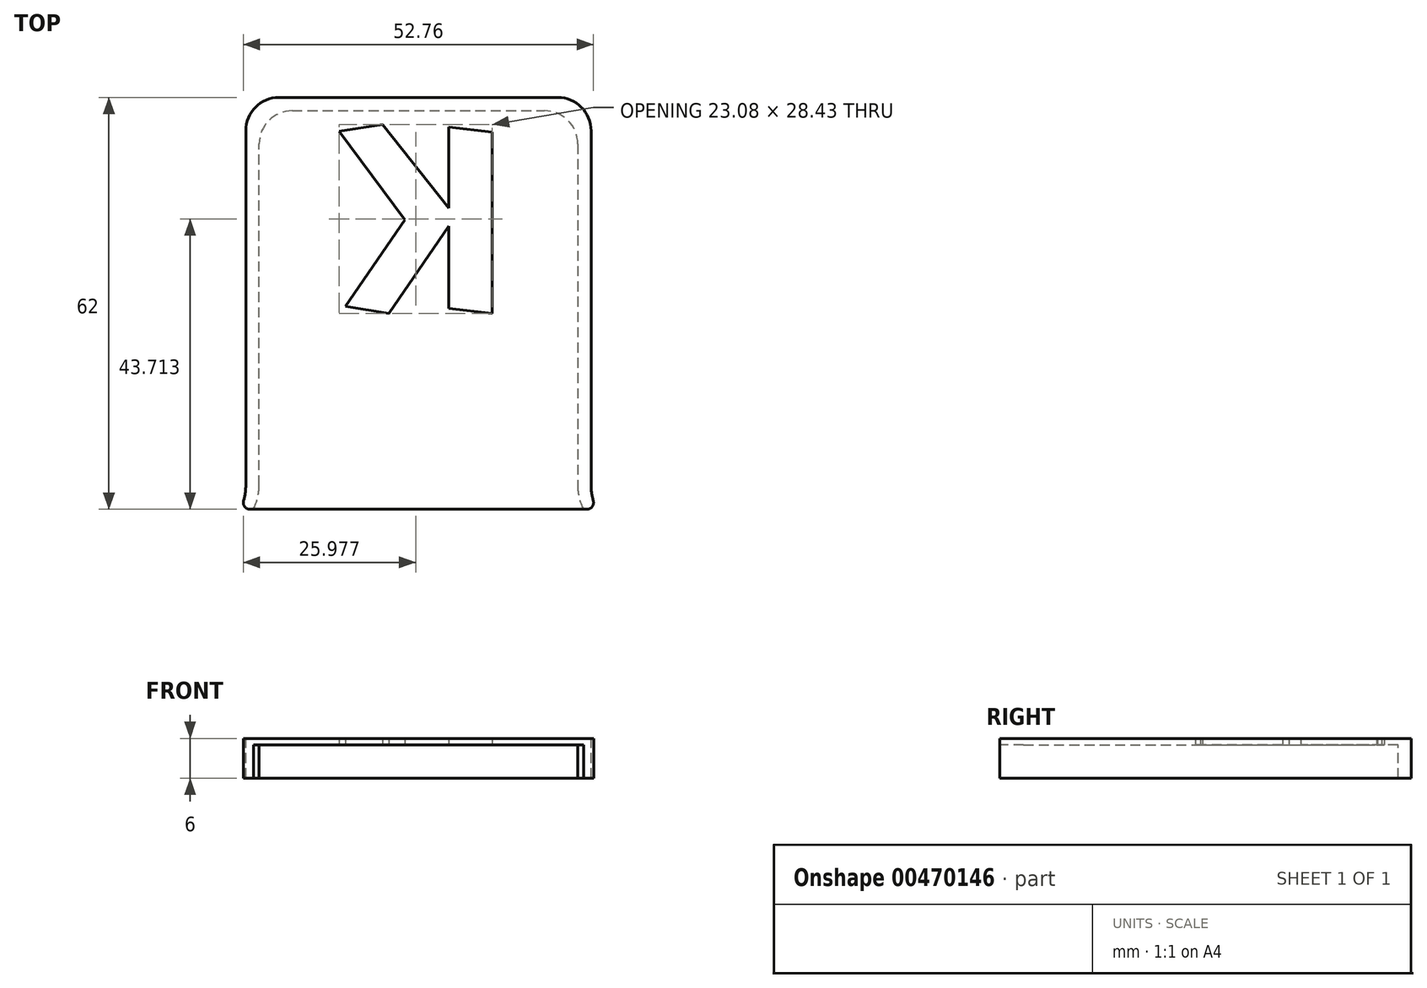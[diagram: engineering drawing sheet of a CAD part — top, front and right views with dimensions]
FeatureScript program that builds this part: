
annotation { "Feature Type Name" : "Feature", "Feature Type Description" : "" }
export const myFeature = defineFeature(function(context is Context, id is Id, definition is map)
    precondition{}
    {
        {
            var Q0;
            Q0=qCreatedBy(makeId("Top.planeOp"),FACE);
            var sketch = newSketch(context, id + "F0", { "sketchPlane" : qUnion([Q0])});
            skLineSegment(sketch, "E0", {"start": v(-24, 30) * mm, "end": v(24, 30) * mm});
            skLineSegment(sketch, "E1", {"start": v(24, 30) * mm, "end": v(24, -30) * mm});
            skLineSegment(sketch, "E2", {"start": v(24, -30) * mm, "end": v(-24, -30) * mm});
            skLineSegment(sketch, "E3", {"start": v(-24, -30) * mm, "end": v(-24, 30) * mm});
            skLineSegment(sketch, "E4", {"start": v(24, 30) * mm, "end": v(-24, -30) * mm, "construction": true});
            skLineSegment(sketch, "E5.MirrorCS", {"start": v(-26.5, -30) * mm, "end": v(-24, -20.3) * mm});
            skLineSegment(sketch, "E6.MirrorCS", {"start": v(-24, -30) * mm, "end": v(-26.5, -30) * mm});
            skLineSegment(sketch, "E7", {"start": v(0, 0) * mm, "end": v(0, 30) * mm, "construction": true});
            skLineSegment(sketch, "E8.MirrorCS", {"start": v(26.5, -30) * mm, "end": v(24, -20.3) * mm});
            skLineSegment(sketch, "E9.MirrorCS", {"start": v(24, -30) * mm, "end": v(26.5, -30) * mm});
            skSolve(sketch);
        }
        {
            var Q0;
            Q0=makeQuery(id+"F0.imprint","IMPRINT",FACE,{"disambiguationData":[TD([[makeQuery(id+"F0.imprint","IMPRINT",EDGE,{"derivedFrom":sQuery(id+"F0.wireOp",EDGE,"E0")}),-1.0]])]});
            var Q1;
            {var subQ0=sQuery(id+"F0.wireOp",EDGE,"ucTv49aQ-58Fh-MB05-3OkK-iMjQsQtgxZcr");Q1=makeQuery(id+"F0.imprint","IMPRINT",FACE,{"disambiguationData":[TD([[makeQuery(id+"F0.imprint","IMPRINT",EDGE,{"derivedFrom":subQ0}),1.0]])]});}
            var Q2;
            {var subQ2=sQuery(id+"F0.wireOp",EDGE,"E5.MirrorCS");Q2=makeQuery(id+"F0.imprint","IMPRINT",FACE,{"disambiguationData":[TD([[makeQuery(id+"F0.imprint","IMPRINT",EDGE,{"derivedFrom":subQ2}),-1.0]])]});}
            var Q3;
            {var subQ2=sQuery(id+"F0.wireOp",EDGE,"E8.MirrorCS");Q3=makeQuery(id+"F0.imprint","IMPRINT",FACE,{"disambiguationData":[TD([[makeQuery(id+"F0.imprint","IMPRINT",EDGE,{"derivedFrom":subQ2}),1.0]])]});}
            extrude(context, id + "F1", {"entities" : qUnion([Q0, Q1, Q2, Q3]), "depth" : 1 * mm});
        }
        {
            var Q0;
            Q0=makeQuery(id+"F1.opExtrude","CAP_FACE",FACE,{"disambiguationData":[OSD([sQuery(id+"F0.wireOp",EDGE,"E0"),sQuery(id+"F0.wireOp",EDGE,"E1"),sQuery(id+"F0.wireOp",EDGE,"E2"),sQuery(id+"F0.wireOp",EDGE,"E3")])],"isStart":false});
            var sketch = newSketch(context, id + "F2", { "sketchPlane" : qUnion([Q0])});
            skLineSegment(sketch, "E10", {"start": v(24, -26.4) * mm, "end": v(24, 30) * mm});
            skLineSegment(sketch, "E11", {"start": v(24, 30) * mm, "end": v(0, 30) * mm});
            skLineSegment(sketch, "E12", {"start": v(0, 32) * mm, "end": v(26, 32) * mm});
            skLineSegment(sketch, "E13", {"start": v(26, 32) * mm, "end": v(26, -26.4) * mm});
            skLineSegment(sketch, "E14", {"start": v(24.85, -30) * mm, "end": v(24.85, -30) * mm});
            skLineSegment(sketch, "E15", {"start": v(24.85, -30) * mm, "end": v(26.85, -30) * mm});
            skLineSegment(sketch, "E16", {"start": v(26.85, -30) * mm, "end": v(26.85, -30) * mm});
            skPoint(sketch, "E17.visualSharp", {"position": v(24, -28.3) * mm});
            skArc(sketch, "E17.filletArc", {"start": v(24, -26.4) * mm, "mid": v(24.22, -28.25) * mm, "end": v(24.85, -30) * mm});
            skPoint(sketch, "E18.visualSharp", {"position": v(26, -28.3) * mm});
            skArc(sketch, "E18.filletArc", {"start": v(26, -26.4) * mm, "mid": v(26.22, -28.25) * mm, "end": v(26.85, -30) * mm});
            skLineSegment(sketch, "E19", {"start": v(0, 0) * mm, "end": v(0, 30) * mm, "construction": true});
            skLineSegment(sketch, "E20.MirrorCS", {"start": v(-24.85, -30) * mm, "end": v(-24.85, -30) * mm});
            skArc(sketch, "E21.MirrorCS", {"start": v(-24, -26.4) * mm, "mid": v(-24.22, -28.25) * mm, "end": v(-24.85, -30) * mm});
            skLineSegment(sketch, "E22.MirrorCS", {"start": v(-26.85, -30) * mm, "end": v(-26.85, -30) * mm});
            skArc(sketch, "E23.MirrorCS", {"start": v(-26, -26.4) * mm, "mid": v(-26.22, -28.25) * mm, "end": v(-26.85, -30) * mm});
            skLineSegment(sketch, "E24.MirrorCS", {"start": v(-24.85, -30) * mm, "end": v(-26.85, -30) * mm});
            skPoint(sketch, "E25.MirrorP", {"position": v(-26, -28.3) * mm});
            skLineSegment(sketch, "E26.MirrorCS", {"start": v(0, 32) * mm, "end": v(-26, 32) * mm});
            skLineSegment(sketch, "E27.MirrorCS", {"start": v(-24, -26.4) * mm, "end": v(-24, 30) * mm});
            skLineSegment(sketch, "E28.MirrorCS", {"start": v(-24, 30) * mm, "end": v(0, 30) * mm});
            skLineSegment(sketch, "E29.MirrorCS", {"start": v(-26, 32) * mm, "end": v(-26, -26.4) * mm});
            skPoint(sketch, "E30.MirrorP", {"position": v(-24, -28.3) * mm});
            skSolve(sketch);
        }
        {
            var Q0;
            Q0=qSketchRegion(id+"F2",true);
            extrude(context, id + "F3", {"entities" : qUnion([Q0]), "operationType" : NewBodyOperationType.ADD, "oppositeDirection" : true, "depth" : 6 * mm});
        }
        {
            var Q0;
            Q0=makeQuery(id+"F3.opExtrude","SWEPT_EDGE",EDGE,{"disambiguationData":[OSD([sQuery(id+"F2.wireOp",EDGE,"E22.MirrorCS"),sQuery(id+"F2.wireOp",EDGE,"E24.MirrorCS")])]});
            var Q1;
            Q1=makeQuery(id+"F3.opExtrude","SWEPT_EDGE",EDGE,{"disambiguationData":[OSD([sQuery(id+"F2.wireOp",EDGE,"E15"),sQuery(id+"F2.wireOp",EDGE,"E16")])]});
            fillet(context, id + "F4", {"entities" : qUnion([Q0, Q1]), "radius" : 1 * mm, "tangentPropagation" : true, "allowEdgeOverflow" : false});
        }
        {
            var Q0;
            Q0=makeQuery(id+"F3.opExtrude","SWEPT_EDGE",EDGE,{"disambiguationData":[OSD([sQuery(id+"F2.wireOp",EDGE,"E10"),sQuery(id+"F2.wireOp",EDGE,"E11")])]});
            var Q1;
            Q1=makeQuery(id+"F3.opExtrude","SWEPT_EDGE",EDGE,{"disambiguationData":[OSD([sQuery(id+"F2.wireOp",EDGE,"E12"),sQuery(id+"F2.wireOp",EDGE,"E13")])]});
            var Q2;
            Q2=makeQuery(id+"F3.opExtrude","SWEPT_EDGE",EDGE,{"disambiguationData":[OSD([sQuery(id+"F2.wireOp",EDGE,"E26.MirrorCS"),sQuery(id+"F2.wireOp",EDGE,"E29.MirrorCS")])]});
            var Q3;
            Q3=makeQuery(id+"F3.opExtrude","SWEPT_EDGE",EDGE,{"disambiguationData":[OSD([sQuery(id+"F2.wireOp",EDGE,"E27.MirrorCS"),sQuery(id+"F2.wireOp",EDGE,"E28.MirrorCS")])]});
            fillet(context, id + "F5", {"entities" : qUnion([Q0, Q1, Q2, Q3]), "radius" : 5 * mm, "tangentPropagation" : true, "allowEdgeOverflow" : false});
        }
        {
            var Q0;
            Q0=makeQuery(id+"F1.opExtrude","CAP_FACE",FACE,{"disambiguationData":[OSD([sQuery(id+"F0.wireOp",EDGE,"E0"),sQuery(id+"F0.wireOp",EDGE,"E1"),sQuery(id+"F0.wireOp",EDGE,"E2"),sQuery(id+"F0.wireOp",EDGE,"E3"),sQuery(id+"F0.wireOp",EDGE,"ucTv49aQ-58Fh-MB05-3OkK-iMjQsQtgxZcr"),sQuery(id+"F0.wireOp",EDGE,"HR3CxZTj-9KNa-pOoI-pPEb-q9pz9odpttWS"),sQuery(id+"F0.wireOp",EDGE,"E5.MirrorCS"),sQuery(id+"F0.wireOp",EDGE,"E6.MirrorCS")])],"isStart":true});
            var sketch = newSketch(context, id + "F6", { "sketchPlane" : qUnion([Q0])});
            skLineSegment(sketch, "E31", {"start": v(24, 0) * mm, "end": v(-24, 0) * mm, "construction": true});
            skLineSegment(sketch, "E32", {"start": v(0, -30) * mm, "end": v(0, 30) * mm, "construction": true});
            skLineSegment(sketch, "E33", {"start": v(11.86, -22.76) * mm, "end": v(11.86, 0) * mm});
            skLineSegment(sketch, "E34", {"start": v(11.86, 0) * mm, "end": v(6.4, -0.63) * mm});
            skLineSegment(sketch, "E35", {"start": v(6.4, -0.63) * mm, "end": v(6.4, -23.39) * mm});
            skLineSegment(sketch, "E36", {"start": v(6.4, -23.39) * mm, "end": v(11.86, -22.76) * mm});
            skLineSegment(sketch, "E37", {"start": v(6.4, -13.22) * mm, "end": v(-1.93, -23.69) * mm});
            skLineSegment(sketch, "E38", {"start": v(-1.93, -23.69) * mm, "end": v(-7.37, -22.87) * mm});
            skLineSegment(sketch, "E39", {"start": v(-7.37, -22.87) * mm, "end": v(0.9, -11.72) * mm});
            skLineSegment(sketch, "E40", {"start": v(0.9, -11.72) * mm, "end": v(-6.56, -0.87) * mm});
            skLineSegment(sketch, "E41", {"start": v(-6.56, -0.87) * mm, "end": v(-1.13, 0) * mm});
            skLineSegment(sketch, "E42", {"start": v(-1.13, 0) * mm, "end": v(6.4, -10.95) * mm});
            skLineSegment(sketch, "E43", {"start": v(6.4, -10.95) * mm, "end": v(6.4, -13.22) * mm});
            skPoint(sketch, "E44", {"position": v(5.21, -12.14) * mm});
            skSolve(sketch);
        }
        {
            var Q0;
            Q0=makeQuery(id+"F6.imprint","IMPRINT",FACE,{"disambiguationData":[TD([[makeQuery(id+"F6.imprint","IMPRINT",EDGE,{"derivedFrom":sQuery(id+"F6.wireOp",EDGE,"E33")}),1.0]])]});
            var Q1;
            {var subQ0=sQuery(id+"F6.wireOp",EDGE,"E37");Q1=makeQuery(id+"F6.imprint","IMPRINT",FACE,{"disambiguationData":[TD([[makeQuery(id+"F6.imprint","IMPRINT",EDGE,{"derivedFrom":subQ0}),-1.0]])]});}
            extrude(context, id + "F7", {"entities" : qUnion([Q0, Q1]), "oppositeDirection" : true, "offsetDistance" : 25 * mm, "depth" : 25 * mm, "symmetric" : true});
        }
        {
            var Q0;
            Q0=makeQuery(id+"F7.opExtrude","SWEPT_BODY",BODY,{"disambiguationData":[OSD([sQuery(id+"F6.wireOp",EDGE,"E33"),sQuery(id+"F6.wireOp",EDGE,"E34"),sQuery(id+"F6.wireOp",EDGE,"E35"),sQuery(id+"F6.wireOp",EDGE,"E36"),sQuery(id+"F6.wireOp",EDGE,"E37"),sQuery(id+"F6.wireOp",EDGE,"E38"),sQuery(id+"F6.wireOp",EDGE,"E39"),sQuery(id+"F6.wireOp",EDGE,"E40"),sQuery(id+"F6.wireOp",EDGE,"E41"),sQuery(id+"F6.wireOp",EDGE,"E42")])]});
            var Q1;
            Q1=qCreatedBy(makeId("Origin.pointOp"),VERTEX);
            transform(context, id + "F8", {"entities" : qUnion([Q0]), "transformType" : TransformType.SCALE_UNIFORMLY, "scale" : 1.2, "scalePoint" : qUnion([Q1]), "makeCopy" : false});
        }
        {
            var Q0;
            Q0=makeQuery(id+"F7.opExtrude","SWEPT_BODY",BODY,{"disambiguationData":[OSD([sQuery(id+"F6.wireOp",EDGE,"E33"),sQuery(id+"F6.wireOp",EDGE,"E34"),sQuery(id+"F6.wireOp",EDGE,"E35"),sQuery(id+"F6.wireOp",EDGE,"E36"),sQuery(id+"F6.wireOp",EDGE,"E37"),sQuery(id+"F6.wireOp",EDGE,"E38"),sQuery(id+"F6.wireOp",EDGE,"E39"),sQuery(id+"F6.wireOp",EDGE,"E40"),sQuery(id+"F6.wireOp",EDGE,"E41"),sQuery(id+"F6.wireOp",EDGE,"E42")])]});
            transform(context, id + "F9", {"entities" : qUnion([Q0]), "transformType" : TransformType.TRANSLATION_3D, "dx" : -3.1 * mm, "dy" : -0.5 * mm, "dz" : 0 * mm, "makeCopy" : false});
        }
        {
            var Q0;
            Q0=makeQuery(id+"F7.opExtrude","SWEPT_BODY",BODY,{"disambiguationData":[OSD([sQuery(id+"F6.wireOp",EDGE,"E33"),sQuery(id+"F6.wireOp",EDGE,"E34"),sQuery(id+"F6.wireOp",EDGE,"E35"),sQuery(id+"F6.wireOp",EDGE,"E36"),sQuery(id+"F6.wireOp",EDGE,"E37"),sQuery(id+"F6.wireOp",EDGE,"E38"),sQuery(id+"F6.wireOp",EDGE,"E39"),sQuery(id+"F6.wireOp",EDGE,"E40"),sQuery(id+"F6.wireOp",EDGE,"E41"),sQuery(id+"F6.wireOp",EDGE,"E42")])]});
            var Q1;
            Q1=makeQuery(id+"F1.opExtrude","SWEPT_BODY",BODY,{"disambiguationData":[OSD([sQuery(id+"F0.wireOp",EDGE,"E0"),sQuery(id+"F0.wireOp",EDGE,"E1"),sQuery(id+"F0.wireOp",EDGE,"E2"),sQuery(id+"F0.wireOp",EDGE,"E3"),sQuery(id+"F0.wireOp",EDGE,"E5.MirrorCS"),sQuery(id+"F0.wireOp",EDGE,"E6.MirrorCS"),sQuery(id+"F0.wireOp",EDGE,"E8.MirrorCS"),sQuery(id+"F0.wireOp",EDGE,"E9.MirrorCS")])]});
            booleanBodies(context, id + "F10", {"operationType" : BooleanOperationType.SUBTRACTION, "tools" : qUnion([Q0]), "targets" : qUnion([Q1])});
        }
    });
